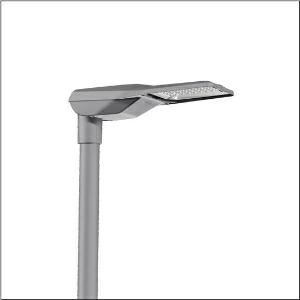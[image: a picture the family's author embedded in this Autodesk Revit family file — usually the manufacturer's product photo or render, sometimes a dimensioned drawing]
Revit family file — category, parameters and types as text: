
# Revit family: streetlight_sl_21_iq_mini___st1_5a_5xe2p31g08gb_08f7
name_source: partatom
category: Lighting Fixtures
units: mm (PartAtom-declared; Revit-internal decimal feet)

## family parameters
Cut with Voids When Loaded = No
Host = Face
Light Source = No
Part Type = Normal
Room Calculation Point = No
Round Connector Dimension = Use Diameter
Shared = No

## types (1)
- --- (1 x LED, 5580 lm, 37.1 W, 3000K)
    Apparent Load = 37 VA
    CIE Flux Codes = 22 53 95 100 100
    Color Rendering = 70
    Color Temperature = 3000K
    Default Elevation = 1800 mm
    Description = Streetlight SL 21 iQ mini, mast luminaire, primary light control with lens, of PMMA, primary optical cover: cover, of toughened safety glass, transparent, light distribution: ST1.5a, light emission: direct distribution, primary light characteristic: asymmetric, installation type: post-top, side-entry, LED, High Power LED, rated luminous flux: 5.580lm, luminous efficacy: 150lm/W, light colour: 730, colour temperature: 3000K, control: Street-Remote, Auto-Match, Temp-Guard, Lumen-Switch, Night-Set, Smart-Wire, Light-Fading, Desk-Remote (wireless, voltage-free reading and setting of iQ features in the workshop via application-optimized NFC function/RFID function), optimised constant luminous flux control (CLO 2.0), presetting dimming linear, mains connection: 220..240V, AC, 50/60Hz, start of lifetime: 37W, end of service life: 39W, reduction: 18W, luminaire housing, of diecast aluminium, powder-coated, Siteco® metallic grey (DB 702S), corrosivity category C5 mid according to DIN EN ISO 12944, please order mast flange separately, inclination adjustable: 0°, 5°, 10°, 15°, sealing non-destructively replaceable, multi-level sealing system, length: 628mm, width: 235mm, height: 110mm, mast flange for spigot size: 42mm (side-entry): 5XC10008XM4, 60/48mm (side-entry/post-top): 5XC10108XM2, 76/60mm (side-entry/post-top): 5XC10108XM1, protection rating (complete): IP66, insulation class (complete): insulation class II (safety insulation), certification: CE, ENEC, ENEC+, VDE, impact resistance: IK09, permissible operating ambient temperature for outdoor applications: -40..+50°C, standard-compliant lighting for roads and squares, packaging unit: 1 piece

Light Distribution: ST1.5a
    Height = 110 mm
    Lamp = 1 x LED
    Lamp Light Flux = 5580 lm
    Lamp Power = 37.1 W
    Lamp count = 1
    Length = 625 mm
    Luminous efficacy = 150 lm/W
    Manufacturer = Siteco
    ModVariant = No
    Model = 5XE2P31G08GB
    Number of Poles = 1
    OnlyDefault = Yes
    Power Factor = 1
    Product Name = Streetlight SL 21 iQ mini | ST1.5a
    Product group = mast luminaire | pylon top
    ProductGroupID = 6100
    Protection Class = Protection class II
    Protection Degree = IP 66
    RLX_Detail_Level = 1
    RLX_Emergency_Light_Flux = 0 lm
    RLX_Emergency_Type = 0
    RLX_Emergency_Type_DB = No
    RlxData = <blob elided: 95609 chars, md5=35a86d21>
    Socket = socket
    Standby Power = 0 W
    System Light Flux = 5580 lm
    System Power = 37 W
    Type Comments = factory setting: luminous flux: 100 % | dim-lin: 254 | 385 mA
    Type Image = l_1003519.jpg
    URL = http://relux.com
    VarID = @adj_126839
    Voltage = 0 V
    Weight = 0.00 kg
    Width = 234 mm

## geometry (parser evidence)
native form markers: Blend x4, Sweep x9
no freeform markers — native parametric forms only
